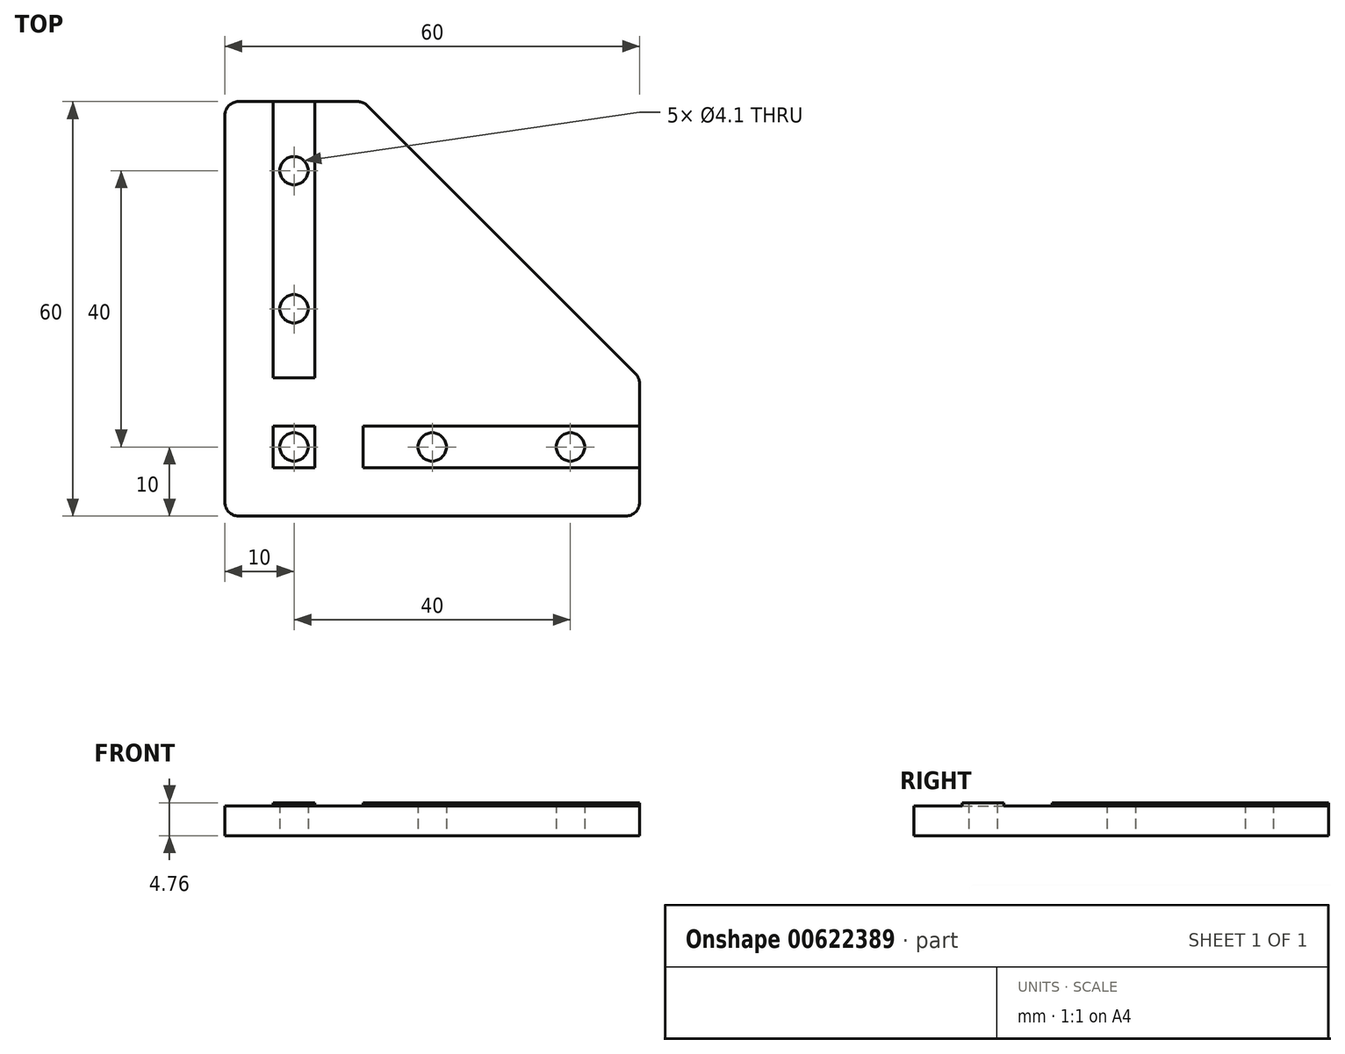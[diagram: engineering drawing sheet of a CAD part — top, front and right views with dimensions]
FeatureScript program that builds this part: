
annotation { "Feature Type Name" : "Feature", "Feature Type Description" : "" }
export const myFeature = defineFeature(function(context is Context, id is Id, definition is map)
    precondition{}
    {
        {
            assignVariable(context, id + "F0", {"name" : "TotalThick", "anyValue" : 4.76});
        }
        {
            assignVariable(context, id + "F1", {"name" : "Recess", "anyValue" : 0.5});
        }
        {
            var Q0;
            Q0=qCreatedBy(makeId("Top.planeOp"),FACE);
            var sketch = newSketch(context, id + "F2", { "sketchPlane" : qUnion([Q0])});
            skLineSegment(sketch, "E0", {"start": v(-10, 50) * mm, "end": v(-10, -10) * mm});
            skLineSegment(sketch, "E1", {"start": v(-10, -10) * mm, "end": v(50, -10) * mm});
            skLineSegment(sketch, "E2", {"start": v(50, -10) * mm, "end": v(50, 10) * mm});
            skLineSegment(sketch, "E3", {"start": v(50, 10) * mm, "end": v(10, 50) * mm});
            skLineSegment(sketch, "E4", {"start": v(10, 50) * mm, "end": v(-10, 50) * mm});
            skCircle(sketch, "E5", {"center": v(0, 0) * mm, "radius": 2.05 * mm});
            skCircle(sketch, "E6", {"center": v(0, 20) * mm, "radius": 2.05 * mm});
            skCircle(sketch, "E7", {"center": v(0, 40) * mm, "radius": 2.05 * mm});
            skCircle(sketch, "E8", {"center": v(20, 0) * mm, "radius": 2.05 * mm});
            skCircle(sketch, "E9", {"center": v(40, 0) * mm, "radius": 2.05 * mm});
            skLineSegment(sketch, "E10", {"start": v(-3.02, 50) * mm, "end": v(-3.03, -10) * mm});
            skLineSegment(sketch, "E11.MirrorCS", {"start": v(3.03, 50) * mm, "end": v(3.02, -10) * mm});
            skLineSegment(sketch, "E12", {"start": v(-10, 3.03) * mm, "end": v(50, 3.02) * mm});
            skLineSegment(sketch, "E13.MirrorCS", {"start": v(-10, -3.03) * mm, "end": v(50, -3.02) * mm});
            skLineSegment(sketch, "E14", {"start": v(10, 50) * mm, "end": v(10, -10) * mm});
            skLineSegment(sketch, "E15", {"start": v(50, 10) * mm, "end": v(-10, 10) * mm});
            skSolve(sketch);
        }
        {
            var Q0;
            Q0 = qSketchRegion(id + "F2", true);
            var Q1;
            {var subQ0=sQuery(id+"F2.wireOp",EDGE,"E15");var subQ1=sQuery(id+"F2.wireOp",EDGE,"E11.MirrorCS");var subQ2=makeQuery(id+"F2.imprint","INTERSECT",VERTEX,{"derivedFrom":[subQ1,subQ0]});Q1=makeQuery(id+"F2.imprint","IMPRINT",FACE,{"disambiguationData":[TD([[makeQuery(id+"F2.imprint","IMPRINT",EDGE,{"disambiguationData":[TD([[subQ2,-1.0]])],"derivedFrom":subQ1}),1.0]])]});}
            var Q2;
            {var subQ0=sQuery(id+"F2.wireOp",EDGE,"E12");var subQ1=sQuery(id+"F2.wireOp",EDGE,"E11.MirrorCS");var subQ2=makeQuery(id+"F2.imprint","INTERSECT",VERTEX,{"derivedFrom":[subQ1,subQ0]});Q2=makeQuery(id+"F2.imprint","IMPRINT",FACE,{"disambiguationData":[TD([[makeQuery(id+"F2.imprint","IMPRINT",EDGE,{"disambiguationData":[TD([[subQ2,-1.0]])],"derivedFrom":subQ1}),1.0]])]});}
            var Q3;
            Q3=makeQuery(id+"F2.imprint","IMPRINT",FACE,{"disambiguationData":[TD([[makeQuery(id+"F2.imprint","IMPRINT",EDGE,{"derivedFrom":sQuery(id+"F2.wireOp",EDGE,"E5")}),-1.0]])]});
            var Q4;
            {var subQ0=sQuery(id+"F2.wireOp",EDGE,"E15");var subQ1=sQuery(id+"F2.wireOp",EDGE,"E10");var subQ2=makeQuery(id+"F2.imprint","INTERSECT",VERTEX,{"derivedFrom":[subQ1,subQ0]});Q4=makeQuery(id+"F2.imprint","IMPRINT",FACE,{"disambiguationData":[TD([[makeQuery(id+"F2.imprint","IMPRINT",EDGE,{"disambiguationData":[TD([[subQ2,-1.0]])],"derivedFrom":subQ1}),1.0]])]});}
            extrude(context, id + "F3", {"entities" : qUnion([Q0, Q1, Q2, Q3, Q4]), "depth" : (getVariable(context, 'TotalThick') - getVariable(context, 'Recess')) * mm, "offsetDistance" : 25 * mm});
        }
        {
            var Q0;
            Q0=makeQuery(id+"F2.imprint","IMPRINT",FACE,{"disambiguationData":[TD([[makeQuery(id+"F2.imprint","IMPRINT",EDGE,{"derivedFrom":sQuery(id+"F2.wireOp",EDGE,"E5")}),-1.0]])]});
            var Q1;
            Q1=makeQuery(id+"F2.imprint","IMPRINT",FACE,{"disambiguationData":[TD([[makeQuery(id+"F2.imprint","IMPRINT",EDGE,{"derivedFrom":sQuery(id+"F2.wireOp",EDGE,"E8")}),-1.0]])]});
            var Q2;
            Q2=makeQuery(id+"F2.imprint","IMPRINT",FACE,{"disambiguationData":[TD([[makeQuery(id+"F2.imprint","IMPRINT",EDGE,{"derivedFrom":sQuery(id+"F2.wireOp",EDGE,"E6")}),-1.0]])]});
            extrude(context, id + "F4", {"entities" : qUnion([Q0, Q1, Q2]), "operationType" : NewBodyOperationType.ADD, "depth" : (getVariable(context, 'TotalThick')) * mm, "offsetDistance" : 25 * mm});
        }
        {
            var Q0;
            Q0=makeQuery(id+"F3.opExtrude","SWEPT_EDGE",EDGE,{"disambiguationData":[OSD([sQuery(id+"F2.wireOp",EDGE,"E2"),sQuery(id+"F2.wireOp",EDGE,"E3"),sQuery(id+"F2.wireOp",EDGE,"E15")])]});
            var Q1;
            Q1=makeQuery(id+"F3.opExtrude","SWEPT_EDGE",EDGE,{"disambiguationData":[OSD([sQuery(id+"F2.wireOp",EDGE,"E1"),sQuery(id+"F2.wireOp",EDGE,"E2")])]});
            var Q2;
            Q2=makeQuery(id+"F3.opExtrude","SWEPT_EDGE",EDGE,{"disambiguationData":[OSD([sQuery(id+"F2.wireOp",EDGE,"E0"),sQuery(id+"F2.wireOp",EDGE,"E1")])]});
            var Q3;
            Q3=makeQuery(id+"F3.opExtrude","SWEPT_EDGE",EDGE,{"disambiguationData":[OSD([sQuery(id+"F2.wireOp",EDGE,"E0"),sQuery(id+"F2.wireOp",EDGE,"E4")])]});
            var Q4;
            Q4=makeQuery(id+"F3.opExtrude","SWEPT_EDGE",EDGE,{"disambiguationData":[OSD([sQuery(id+"F2.wireOp",EDGE,"E3"),sQuery(id+"F2.wireOp",EDGE,"E4"),sQuery(id+"F2.wireOp",EDGE,"E14")])]});
            fillet(context, id + "F5", {"entities" : qUnion([Q0, Q1, Q2, Q3, Q4]), "radius" : 2 * mm, "tangentPropagation" : true, "allowEdgeOverflow" : false});
        }
    });
